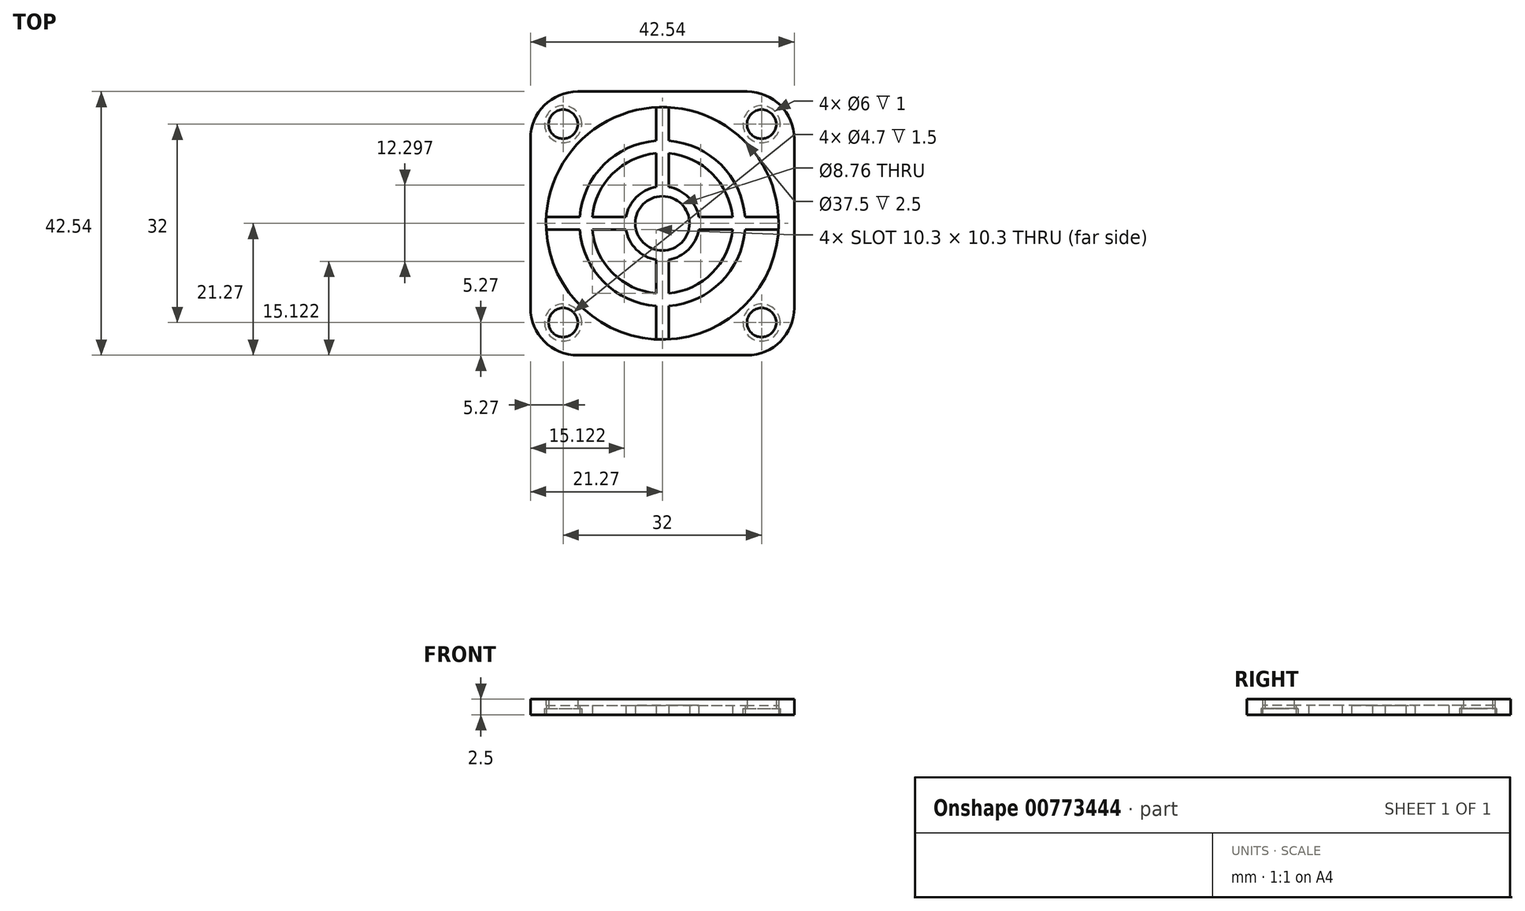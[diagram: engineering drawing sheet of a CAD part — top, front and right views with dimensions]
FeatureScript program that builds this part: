
annotation { "Feature Type Name" : "Feature", "Feature Type Description" : "" }
export const myFeature = defineFeature(function(context is Context, id is Id, definition is map)
    precondition{}
    {
        {
            var Q0;
            Q0=qCreatedBy(makeId("Top.planeOp"),FACE);
            var sketch = newSketch(context, id + "F0", { "sketchPlane" : qUnion([Q0])});
            skCircle(sketch, "E0", {"center": v(-16, 16) * mm, "radius": 1.6 * mm});
            skCircle(sketch, "E1", {"center": v(16, 16) * mm, "radius": 1.6 * mm});
            skCircle(sketch, "E2", {"center": v(16, -16) * mm, "radius": 1.6 * mm});
            skCircle(sketch, "E3", {"center": v(-16, -16) * mm, "radius": 1.6 * mm});
            skLineSegment(sketch, "E4.bottom", {"start": v(-13.65, 20) * mm, "end": v(13.65, 20) * mm});
            skLineSegment(sketch, "E4.top", {"start": v(-13.65, -20) * mm, "end": v(13.65, -20) * mm});
            skLineSegment(sketch, "E4.left", {"start": v(-20, 13.65) * mm, "end": v(-20, -13.65) * mm});
            skLineSegment(sketch, "E4.right", {"start": v(20, 13.65) * mm, "end": v(20, -13.65) * mm});
            skArc(sketch, "E5", {"start": v(-1, 18.72) * mm, "mid": v(-13.26, 13.26) * mm, "end": v(-18.72, 1) * mm});
            skLineSegment(sketch, "E6", {"start": v(-1, 18.72) * mm, "end": v(-1, 13.33) * mm});
            skLineSegment(sketch, "E7", {"start": v(1, 18.72) * mm, "end": v(1, 13.33) * mm});
            skLineSegment(sketch, "E8", {"start": v(-18.72, 1) * mm, "end": v(-13.33, 1) * mm});
            skLineSegment(sketch, "E9", {"start": v(-18.72, -1) * mm, "end": v(-13.33, -1) * mm});
            skArc(sketch, "E10.trimOffspring", {"start": v(18.72, 1) * mm, "mid": v(13.26, 13.26) * mm, "end": v(1, 18.72) * mm});
            skArc(sketch, "E11.trimOffspring", {"start": v(-18.72, -1) * mm, "mid": v(-13.26, -13.26) * mm, "end": v(-1, -18.72) * mm});
            skArc(sketch, "E12.trimOffspring", {"start": v(1, -18.72) * mm, "mid": v(13.26, -13.26) * mm, "end": v(18.72, -1) * mm});
            skArc(sketch, "E13", {"start": v(5.87, 1) * mm, "mid": v(4.21, 4.21) * mm, "end": v(1, 5.87) * mm});
            skArc(sketch, "E14", {"start": v(-1, 11.3) * mm, "mid": v(-8.02, 8.02) * mm, "end": v(-11.3, 1) * mm});
            skArc(sketch, "E15", {"start": v(-1, 13.33) * mm, "mid": v(-9.45, 9.45) * mm, "end": v(-13.33, 1) * mm});
            skLineSegment(sketch, "E16.trimOffspring", {"start": v(-1, 11.3) * mm, "end": v(-1, 5.87) * mm});
            skLineSegment(sketch, "E17.trimOffspring", {"start": v(1, 11.3) * mm, "end": v(1, 5.87) * mm});
            skLineSegment(sketch, "E18.trimOffspring", {"start": v(13.33, 1) * mm, "end": v(18.72, 1) * mm});
            skLineSegment(sketch, "E19.trimOffspring", {"start": v(13.33, -1) * mm, "end": v(18.72, -1) * mm});
            skArc(sketch, "E20.trimOffspring", {"start": v(11.3, 1) * mm, "mid": v(8.02, 8.02) * mm, "end": v(1, 11.3) * mm});
            skArc(sketch, "E21.trimOffspring", {"start": v(13.33, 1) * mm, "mid": v(9.45, 9.45) * mm, "end": v(1, 13.33) * mm});
            skLineSegment(sketch, "E22.trimOffspring", {"start": v(5.87, 1) * mm, "end": v(11.3, 1) * mm});
            skLineSegment(sketch, "E23.trimOffspring", {"start": v(5.87, -1) * mm, "end": v(11.3, -1) * mm});
            skArc(sketch, "E24.trimOffspring", {"start": v(1, -5.87) * mm, "mid": v(4.21, -4.21) * mm, "end": v(5.87, -1) * mm});
            skLineSegment(sketch, "E25.trimOffspring", {"start": v(1, -5.87) * mm, "end": v(1, -11.3) * mm});
            skLineSegment(sketch, "E26.trimOffspring", {"start": v(-1, -5.87) * mm, "end": v(-1, -11.3) * mm});
            skArc(sketch, "E27.trimOffspring", {"start": v(-5.87, -1) * mm, "mid": v(-4.21, -4.21) * mm, "end": v(-1, -5.87) * mm});
            skLineSegment(sketch, "E28.trimOffspring", {"start": v(-11.3, 1) * mm, "end": v(-5.87, 1) * mm});
            skArc(sketch, "E29.trimOffspring", {"start": v(-11.3, -1) * mm, "mid": v(-8.02, -8.02) * mm, "end": v(-1, -11.3) * mm});
            skArc(sketch, "E30.trimOffspring", {"start": v(-13.33, -1) * mm, "mid": v(-9.45, -9.45) * mm, "end": v(-1, -13.33) * mm});
            skLineSegment(sketch, "E31.trimOffspring", {"start": v(-11.3, -1) * mm, "end": v(-5.87, -1) * mm});
            skArc(sketch, "E32.trimOffspring", {"start": v(1, -11.3) * mm, "mid": v(8.02, -8.02) * mm, "end": v(11.3, -1) * mm});
            skArc(sketch, "E33.trimOffspring", {"start": v(1, -13.33) * mm, "mid": v(9.45, -9.45) * mm, "end": v(13.33, -1) * mm});
            skLineSegment(sketch, "E34.trimOffspring", {"start": v(1, -13.33) * mm, "end": v(1, -18.72) * mm});
            skLineSegment(sketch, "E35.trimOffspring", {"start": v(-1, -13.33) * mm, "end": v(-1, -18.72) * mm});
            skArc(sketch, "E36.trimOffspring", {"start": v(-1, 5.87) * mm, "mid": v(-4.21, 4.21) * mm, "end": v(-5.87, 1) * mm});
            skCircle(sketch, "E37", {"center": v(0, 0) * mm, "radius": 4.38 * mm});
            skPoint(sketch, "E38.visualSharp", {"position": v(-20, 20) * mm});
            skArc(sketch, "E38.filletArc", {"start": v(-13.65, 20) * mm, "mid": v(-18.14, 18.14) * mm, "end": v(-20, 13.65) * mm});
            skPoint(sketch, "E39.visualSharp", {"position": v(-20, -20) * mm});
            skArc(sketch, "E39.filletArc", {"start": v(-20, -13.65) * mm, "mid": v(-18.14, -18.14) * mm, "end": v(-13.65, -20) * mm});
            skPoint(sketch, "E40.visualSharp", {"position": v(20, -20) * mm});
            skArc(sketch, "E40.filletArc", {"start": v(13.65, -20) * mm, "mid": v(18.14, -18.14) * mm, "end": v(20, -13.65) * mm});
            skPoint(sketch, "E41.visualSharp", {"position": v(20, 20) * mm});
            skArc(sketch, "E41.filletArc", {"start": v(20, 13.65) * mm, "mid": v(18.14, 18.14) * mm, "end": v(13.65, 20) * mm});
            skSolve(sketch);
        }
        {
            var Q0;
            Q0=qSketchRegion(id+"F0",true);
            extrude(context, id + "F1", {"entities" : qUnion([Q0]), "depth" : 2.5 * mm, "offsetDistance" : 25.4 * mm});
        }
        {
            var Q0;
            Q0=makeQuery(id+"F1.opExtrude","CAP_FACE",FACE,{"disambiguationData":[OSD([sQuery(id+"F0.wireOp",EDGE,"E0"),sQuery(id+"F0.wireOp",EDGE,"E1"),sQuery(id+"F0.wireOp",EDGE,"E2"),sQuery(id+"F0.wireOp",EDGE,"E3"),sQuery(id+"F0.wireOp",EDGE,"E4.bottom"),sQuery(id+"F0.wireOp",EDGE,"E4.top"),sQuery(id+"F0.wireOp",EDGE,"E4.left"),sQuery(id+"F0.wireOp",EDGE,"E4.right"),sQuery(id+"F0.wireOp",EDGE,"E5"),sQuery(id+"F0.wireOp",EDGE,"E6"),sQuery(id+"F0.wireOp",EDGE,"E7"),sQuery(id+"F0.wireOp",EDGE,"E8"),sQuery(id+"F0.wireOp",EDGE,"E9"),sQuery(id+"F0.wireOp",EDGE,"3f5c4570-0d0e-4342-8f31-e9b691c76b48.trimOffspring"),sQuery(id+"F0.wireOp",EDGE,"b0981ca9-4a93-40c7-8ede-b21ccdf9ea9c.trimOffspring"),sQuery(id+"F0.wireOp",EDGE,"156f85e7-4a59-4eaa-8c94-7897f76e2177.trimOffspring"),sQuery(id+"F0.wireOp",EDGE,"7a4ee4ac-a209-40c9-a21d-254fe2efd8aa.trimOffspring"),sQuery(id+"F0.wireOp",EDGE,"E10.trimOffspring"),sQuery(id+"F0.wireOp",EDGE,"E11.trimOffspring"),sQuery(id+"F0.wireOp",EDGE,"E12.trimOffspring"),sQuery(id+"F0.wireOp",EDGE,"hUL42VZN-iO2z-RDmx-ddcc-wAsxaYuwDb2i"),sQuery(id+"F0.wireOp",EDGE,"E13"),sQuery(id+"F0.wireOp",EDGE,"E14"),sQuery(id+"F0.wireOp",EDGE,"E15"),sQuery(id+"F0.wireOp",EDGE,"E16.trimOffspring"),sQuery(id+"F0.wireOp",EDGE,"E17.trimOffspring"),sQuery(id+"F0.wireOp",EDGE,"E18.trimOffspring"),sQuery(id+"F0.wireOp",EDGE,"E19.trimOffspring"),sQuery(id+"F0.wireOp",EDGE,"E20.trimOffspring"),sQuery(id+"F0.wireOp",EDGE,"E21.trimOffspring"),sQuery(id+"F0.wireOp",EDGE,"E22.trimOffspring"),sQuery(id+"F0.wireOp",EDGE,"E23.trimOffspring"),sQuery(id+"F0.wireOp",EDGE,"E24.trimOffspring"),sQuery(id+"F0.wireOp",EDGE,"5baa72d9-31dc-45eb-b5c1-436ed97127be.trimOffspring"),sQuery(id+"F0.wireOp",EDGE,"E25.trimOffspring"),sQuery(id+"F0.wireOp",EDGE,"E26.trimOffspring"),sQuery(id+"F0.wireOp",EDGE,"923efe1c-8501-4d4e-8851-86086e94e9f1.trimOffspring"),sQuery(id+"F0.wireOp",EDGE,"3f79d5fb-0a8b-4b1f-bc07-6d58af1cd0cc.trimOffspring"),sQuery(id+"F0.wireOp",EDGE,"E27.trimOffspring"),sQuery(id+"F0.wireOp",EDGE,"26bf0d5e-ea2e-47a8-97aa-4e4c95460ec9.trimOffspring"),sQuery(id+"F0.wireOp",EDGE,"E28.trimOffspring"),sQuery(id+"F0.wireOp",EDGE,"E29.trimOffspring"),sQuery(id+"F0.wireOp",EDGE,"E30.trimOffspring"),sQuery(id+"F0.wireOp",EDGE,"E31.trimOffspring"),sQuery(id+"F0.wireOp",EDGE,"E32.trimOffspring"),sQuery(id+"F0.wireOp",EDGE,"E33.trimOffspring"),sQuery(id+"F0.wireOp",EDGE,"E34.trimOffspring"),sQuery(id+"F0.wireOp",EDGE,"E35.trimOffspring"),sQuery(id+"F0.wireOp",EDGE,"E36.trimOffspring"),sQuery(id+"F0.wireOp",EDGE,"6d97bbf4-c9fc-463e-bf00-e0ef0d70c1c3.trimOffspring"),sQuery(id+"F0.wireOp",EDGE,"3c499df6-884c-4b4b-8284-fedb37a8e2a6.trimOffspring"),sQuery(id+"F0.wireOp",EDGE,"9bf78612-3a2b-4ab4-ae83-326c1b6aaf60.trimOffspring")])],"isStart":false});
            var sketch = newSketch(context, id + "F2", { "sketchPlane" : qUnion([Q0])});
            skArc(sketch, "E42.0", {"start": v(-1, 18.72) * mm, "mid": v(-13.26, 13.26) * mm, "end": v(-18.72, 1) * mm});
            skArc(sketch, "E43.0", {"start": v(-18.72, -1) * mm, "mid": v(-13.26, -13.26) * mm, "end": v(-1, -18.72) * mm});
            skCircle(sketch, "E44", {"center": v(0, 0) * mm, "radius": 18.75 * mm});
            skSolve(sketch);
        }
        {
            var Q0;
            Q0=qSketchRegion(id+"F2",true);
            extrude(context, id + "F3", {"entities" : qUnion([Q0]), "operationType" : NewBodyOperationType.REMOVE, "oppositeDirection" : true, "depth" : 1 * mm, "offsetDistance" : 25.4 * mm});
        }
        {
            var Q0;
            Q0=makeQuery(id+"F1.opExtrude","CAP_FACE",FACE,{"disambiguationData":[OSD([sQuery(id+"F0.wireOp",EDGE,"E0"),sQuery(id+"F0.wireOp",EDGE,"E1"),sQuery(id+"F0.wireOp",EDGE,"E2"),sQuery(id+"F0.wireOp",EDGE,"E3"),sQuery(id+"F0.wireOp",EDGE,"E4.bottom"),sQuery(id+"F0.wireOp",EDGE,"E4.top"),sQuery(id+"F0.wireOp",EDGE,"E4.left"),sQuery(id+"F0.wireOp",EDGE,"E4.right"),sQuery(id+"F0.wireOp",EDGE,"E5"),sQuery(id+"F0.wireOp",EDGE,"E6"),sQuery(id+"F0.wireOp",EDGE,"E7"),sQuery(id+"F0.wireOp",EDGE,"E8"),sQuery(id+"F0.wireOp",EDGE,"E9"),sQuery(id+"F0.wireOp",EDGE,"3f5c4570-0d0e-4342-8f31-e9b691c76b48.trimOffspring"),sQuery(id+"F0.wireOp",EDGE,"b0981ca9-4a93-40c7-8ede-b21ccdf9ea9c.trimOffspring"),sQuery(id+"F0.wireOp",EDGE,"156f85e7-4a59-4eaa-8c94-7897f76e2177.trimOffspring"),sQuery(id+"F0.wireOp",EDGE,"7a4ee4ac-a209-40c9-a21d-254fe2efd8aa.trimOffspring"),sQuery(id+"F0.wireOp",EDGE,"E10.trimOffspring"),sQuery(id+"F0.wireOp",EDGE,"E11.trimOffspring"),sQuery(id+"F0.wireOp",EDGE,"E12.trimOffspring"),sQuery(id+"F0.wireOp",EDGE,"hUL42VZN-iO2z-RDmx-ddcc-wAsxaYuwDb2i"),sQuery(id+"F0.wireOp",EDGE,"E13"),sQuery(id+"F0.wireOp",EDGE,"E14"),sQuery(id+"F0.wireOp",EDGE,"E15"),sQuery(id+"F0.wireOp",EDGE,"E16.trimOffspring"),sQuery(id+"F0.wireOp",EDGE,"E17.trimOffspring"),sQuery(id+"F0.wireOp",EDGE,"E18.trimOffspring"),sQuery(id+"F0.wireOp",EDGE,"E19.trimOffspring"),sQuery(id+"F0.wireOp",EDGE,"E20.trimOffspring"),sQuery(id+"F0.wireOp",EDGE,"E21.trimOffspring"),sQuery(id+"F0.wireOp",EDGE,"E22.trimOffspring"),sQuery(id+"F0.wireOp",EDGE,"E23.trimOffspring"),sQuery(id+"F0.wireOp",EDGE,"E24.trimOffspring"),sQuery(id+"F0.wireOp",EDGE,"5baa72d9-31dc-45eb-b5c1-436ed97127be.trimOffspring"),sQuery(id+"F0.wireOp",EDGE,"E25.trimOffspring"),sQuery(id+"F0.wireOp",EDGE,"E26.trimOffspring"),sQuery(id+"F0.wireOp",EDGE,"923efe1c-8501-4d4e-8851-86086e94e9f1.trimOffspring"),sQuery(id+"F0.wireOp",EDGE,"3f79d5fb-0a8b-4b1f-bc07-6d58af1cd0cc.trimOffspring"),sQuery(id+"F0.wireOp",EDGE,"E27.trimOffspring"),sQuery(id+"F0.wireOp",EDGE,"26bf0d5e-ea2e-47a8-97aa-4e4c95460ec9.trimOffspring"),sQuery(id+"F0.wireOp",EDGE,"E28.trimOffspring"),sQuery(id+"F0.wireOp",EDGE,"E29.trimOffspring"),sQuery(id+"F0.wireOp",EDGE,"E30.trimOffspring"),sQuery(id+"F0.wireOp",EDGE,"E31.trimOffspring"),sQuery(id+"F0.wireOp",EDGE,"E32.trimOffspring"),sQuery(id+"F0.wireOp",EDGE,"E33.trimOffspring"),sQuery(id+"F0.wireOp",EDGE,"E34.trimOffspring"),sQuery(id+"F0.wireOp",EDGE,"E35.trimOffspring"),sQuery(id+"F0.wireOp",EDGE,"E36.trimOffspring"),sQuery(id+"F0.wireOp",EDGE,"6d97bbf4-c9fc-463e-bf00-e0ef0d70c1c3.trimOffspring"),sQuery(id+"F0.wireOp",EDGE,"3c499df6-884c-4b4b-8284-fedb37a8e2a6.trimOffspring"),sQuery(id+"F0.wireOp",EDGE,"9bf78612-3a2b-4ab4-ae83-326c1b6aaf60.trimOffspring")])],"isStart":true});
            var sketch = newSketch(context, id + "F4", { "sketchPlane" : qUnion([Q0])});
            skCircle(sketch, "E45.0", {"center": v(-16, -16) * mm, "radius": 1.6 * mm});
            skCircle(sketch, "E46.0", {"center": v(16, -16) * mm, "radius": 1.6 * mm});
            skCircle(sketch, "E47.0", {"center": v(16, 16) * mm, "radius": 1.6 * mm});
            skCircle(sketch, "E48.0", {"center": v(-16, 16) * mm, "radius": 1.6 * mm});
            skCircle(sketch, "E49", {"center": v(-16, 16) * mm, "radius": 3 * mm});
            skCircle(sketch, "E50", {"center": v(16, 16) * mm, "radius": 3 * mm});
            skCircle(sketch, "E51", {"center": v(16, -16) * mm, "radius": 3 * mm});
            skCircle(sketch, "E52", {"center": v(-16, -16) * mm, "radius": 3 * mm});
            skSolve(sketch);
        }
        {
            var Q0;
            Q0=qSketchRegion(id+"F4",true);
            extrude(context, id + "F5", {"entities" : qUnion([Q0]), "operationType" : NewBodyOperationType.REMOVE, "oppositeDirection" : true, "depth" : 1 * mm, "offsetDistance" : 25.4 * mm});
        }
        {
            var Q0;
            Q0=makeQuery(id+"F1.opExtrude","CAP_FACE",FACE,{"disambiguationData":[OSD([sQuery(id+"F0.wireOp",EDGE,"E0"),sQuery(id+"F0.wireOp",EDGE,"E1"),sQuery(id+"F0.wireOp",EDGE,"E2"),sQuery(id+"F0.wireOp",EDGE,"E3"),sQuery(id+"F0.wireOp",EDGE,"E4.bottom"),sQuery(id+"F0.wireOp",EDGE,"E4.top"),sQuery(id+"F0.wireOp",EDGE,"E4.left"),sQuery(id+"F0.wireOp",EDGE,"E4.right"),sQuery(id+"F0.wireOp",EDGE,"E5"),sQuery(id+"F0.wireOp",EDGE,"E6"),sQuery(id+"F0.wireOp",EDGE,"E7"),sQuery(id+"F0.wireOp",EDGE,"E8"),sQuery(id+"F0.wireOp",EDGE,"E9"),sQuery(id+"F0.wireOp",EDGE,"E10.trimOffspring"),sQuery(id+"F0.wireOp",EDGE,"E11.trimOffspring"),sQuery(id+"F0.wireOp",EDGE,"E12.trimOffspring"),sQuery(id+"F0.wireOp",EDGE,"E13"),sQuery(id+"F0.wireOp",EDGE,"E14"),sQuery(id+"F0.wireOp",EDGE,"E15"),sQuery(id+"F0.wireOp",EDGE,"E16.trimOffspring"),sQuery(id+"F0.wireOp",EDGE,"E17.trimOffspring"),sQuery(id+"F0.wireOp",EDGE,"E18.trimOffspring"),sQuery(id+"F0.wireOp",EDGE,"E19.trimOffspring"),sQuery(id+"F0.wireOp",EDGE,"E20.trimOffspring"),sQuery(id+"F0.wireOp",EDGE,"E21.trimOffspring"),sQuery(id+"F0.wireOp",EDGE,"E22.trimOffspring"),sQuery(id+"F0.wireOp",EDGE,"E23.trimOffspring"),sQuery(id+"F0.wireOp",EDGE,"E24.trimOffspring"),sQuery(id+"F0.wireOp",EDGE,"E25.trimOffspring"),sQuery(id+"F0.wireOp",EDGE,"E26.trimOffspring"),sQuery(id+"F0.wireOp",EDGE,"E27.trimOffspring"),sQuery(id+"F0.wireOp",EDGE,"E28.trimOffspring"),sQuery(id+"F0.wireOp",EDGE,"E29.trimOffspring"),sQuery(id+"F0.wireOp",EDGE,"E30.trimOffspring"),sQuery(id+"F0.wireOp",EDGE,"E31.trimOffspring"),sQuery(id+"F0.wireOp",EDGE,"E32.trimOffspring"),sQuery(id+"F0.wireOp",EDGE,"E33.trimOffspring"),sQuery(id+"F0.wireOp",EDGE,"E34.trimOffspring"),sQuery(id+"F0.wireOp",EDGE,"E35.trimOffspring"),sQuery(id+"F0.wireOp",EDGE,"E36.trimOffspring"),sQuery(id+"F0.wireOp",EDGE,"E37"),sQuery(id+"F0.wireOp",EDGE,"E38.filletArc"),sQuery(id+"F0.wireOp",EDGE,"E39.filletArc"),sQuery(id+"F0.wireOp",EDGE,"E40.filletArc"),sQuery(id+"F0.wireOp",EDGE,"E41.filletArc")])],"isStart":true});
            var sketch = newSketch(context, id + "F6", { "sketchPlane" : qUnion([Q0])});
            skLineSegment(sketch, "E53.0", {"start": v(-13.65, 20) * mm, "end": v(13.65, 20) * mm});
            skArc(sketch, "E54.0", {"start": v(-20, 13.65) * mm, "mid": v(-18.14, 18.14) * mm, "end": v(-13.65, 20) * mm});
            skLineSegment(sketch, "E55.0", {"start": v(-20, -13.65) * mm, "end": v(-20, 13.65) * mm});
            skArc(sketch, "E56.0", {"start": v(-13.65, -20) * mm, "mid": v(-18.14, -18.14) * mm, "end": v(-20, -13.65) * mm});
            skLineSegment(sketch, "E57.0", {"start": v(-13.65, -20) * mm, "end": v(13.65, -20) * mm});
            skArc(sketch, "E58.0", {"start": v(20, -13.65) * mm, "mid": v(18.14, -18.14) * mm, "end": v(13.65, -20) * mm});
            skLineSegment(sketch, "E59.0", {"start": v(20, -13.65) * mm, "end": v(20, 13.65) * mm});
            skArc(sketch, "E60.0", {"start": v(13.65, 20) * mm, "mid": v(18.14, 18.14) * mm, "end": v(20, 13.65) * mm});
            skArc(sketch, "E61.0", {"start": v(-21.27, 13.65) * mm, "mid": v(-19.04, 19.04) * mm, "end": v(-13.65, 21.27) * mm});
            skLineSegment(sketch, "E61.1", {"start": v(-21.27, -13.65) * mm, "end": v(-21.27, 13.65) * mm});
            skLineSegment(sketch, "E61.2", {"start": v(-13.65, 21.27) * mm, "end": v(13.65, 21.27) * mm});
            skArc(sketch, "E61.3", {"start": v(-13.65, -21.27) * mm, "mid": v(-19.04, -19.04) * mm, "end": v(-21.27, -13.65) * mm});
            skArc(sketch, "E61.4", {"start": v(13.65, 21.27) * mm, "mid": v(19.04, 19.04) * mm, "end": v(21.27, 13.65) * mm});
            skLineSegment(sketch, "E61.5", {"start": v(21.27, -13.65) * mm, "end": v(21.27, 13.65) * mm});
            skArc(sketch, "E61.6", {"start": v(21.27, -13.65) * mm, "mid": v(19.04, -19.04) * mm, "end": v(13.65, -21.27) * mm});
            skLineSegment(sketch, "E61.7", {"start": v(-13.65, -21.27) * mm, "end": v(13.65, -21.27) * mm});
            skSolve(sketch);
        }
        {
            var Q0;
            Q0=qSketchRegion(id+"F6",true);
            var Q1;
            Q1=makeQuery(id+"F1.opExtrude","CAP_FACE",FACE,{"disambiguationData":[OSD([sQuery(id+"F0.wireOp",EDGE,"E0"),sQuery(id+"F0.wireOp",EDGE,"E1"),sQuery(id+"F0.wireOp",EDGE,"E2"),sQuery(id+"F0.wireOp",EDGE,"E3"),sQuery(id+"F0.wireOp",EDGE,"E4.bottom"),sQuery(id+"F0.wireOp",EDGE,"E4.top"),sQuery(id+"F0.wireOp",EDGE,"E4.left"),sQuery(id+"F0.wireOp",EDGE,"E4.right"),sQuery(id+"F0.wireOp",EDGE,"E5"),sQuery(id+"F0.wireOp",EDGE,"E6"),sQuery(id+"F0.wireOp",EDGE,"E7"),sQuery(id+"F0.wireOp",EDGE,"E8"),sQuery(id+"F0.wireOp",EDGE,"E9"),sQuery(id+"F0.wireOp",EDGE,"E10.trimOffspring"),sQuery(id+"F0.wireOp",EDGE,"E11.trimOffspring"),sQuery(id+"F0.wireOp",EDGE,"E12.trimOffspring"),sQuery(id+"F0.wireOp",EDGE,"E13"),sQuery(id+"F0.wireOp",EDGE,"E14"),sQuery(id+"F0.wireOp",EDGE,"E15"),sQuery(id+"F0.wireOp",EDGE,"E16.trimOffspring"),sQuery(id+"F0.wireOp",EDGE,"E17.trimOffspring"),sQuery(id+"F0.wireOp",EDGE,"E18.trimOffspring"),sQuery(id+"F0.wireOp",EDGE,"E19.trimOffspring"),sQuery(id+"F0.wireOp",EDGE,"E20.trimOffspring"),sQuery(id+"F0.wireOp",EDGE,"E21.trimOffspring"),sQuery(id+"F0.wireOp",EDGE,"E22.trimOffspring"),sQuery(id+"F0.wireOp",EDGE,"E23.trimOffspring"),sQuery(id+"F0.wireOp",EDGE,"E24.trimOffspring"),sQuery(id+"F0.wireOp",EDGE,"E25.trimOffspring"),sQuery(id+"F0.wireOp",EDGE,"E26.trimOffspring"),sQuery(id+"F0.wireOp",EDGE,"E27.trimOffspring"),sQuery(id+"F0.wireOp",EDGE,"E28.trimOffspring"),sQuery(id+"F0.wireOp",EDGE,"E29.trimOffspring"),sQuery(id+"F0.wireOp",EDGE,"E30.trimOffspring"),sQuery(id+"F0.wireOp",EDGE,"E31.trimOffspring"),sQuery(id+"F0.wireOp",EDGE,"E32.trimOffspring"),sQuery(id+"F0.wireOp",EDGE,"E33.trimOffspring"),sQuery(id+"F0.wireOp",EDGE,"E34.trimOffspring"),sQuery(id+"F0.wireOp",EDGE,"E35.trimOffspring"),sQuery(id+"F0.wireOp",EDGE,"E36.trimOffspring"),sQuery(id+"F0.wireOp",EDGE,"E37"),sQuery(id+"F0.wireOp",EDGE,"E38.filletArc"),sQuery(id+"F0.wireOp",EDGE,"E39.filletArc"),sQuery(id+"F0.wireOp",EDGE,"E40.filletArc"),sQuery(id+"F0.wireOp",EDGE,"E41.filletArc")])],"isStart":false});
            extrude(context, id + "F7", {"entities" : qUnion([Q0]), "operationType" : NewBodyOperationType.ADD, "endBound" : BoundingType.UP_TO_SURFACE, "oppositeDirection" : true, "depth" : 25.4 * mm, "endBoundEntityFace" : qUnion([Q1]), "offsetDistance" : 25.4 * mm});
        }
        {
            var Q0;
            Q0=makeQuery(id+"F7.boolean.opBoolean","MERGE",FACE,{"derivedFrom":[makeQuery(id+"F1.opExtrude","CAP_FACE",FACE,{"disambiguationData":[OSD([sQuery(id+"F0.wireOp",EDGE,"E0"),sQuery(id+"F0.wireOp",EDGE,"E1"),sQuery(id+"F0.wireOp",EDGE,"E2"),sQuery(id+"F0.wireOp",EDGE,"E3"),sQuery(id+"F0.wireOp",EDGE,"E4.bottom"),sQuery(id+"F0.wireOp",EDGE,"E4.top"),sQuery(id+"F0.wireOp",EDGE,"E4.left"),sQuery(id+"F0.wireOp",EDGE,"E4.right"),sQuery(id+"F0.wireOp",EDGE,"E5"),sQuery(id+"F0.wireOp",EDGE,"E6"),sQuery(id+"F0.wireOp",EDGE,"E7"),sQuery(id+"F0.wireOp",EDGE,"E8"),sQuery(id+"F0.wireOp",EDGE,"E9"),sQuery(id+"F0.wireOp",EDGE,"E10.trimOffspring"),sQuery(id+"F0.wireOp",EDGE,"E11.trimOffspring"),sQuery(id+"F0.wireOp",EDGE,"E12.trimOffspring"),sQuery(id+"F0.wireOp",EDGE,"E13"),sQuery(id+"F0.wireOp",EDGE,"E14"),sQuery(id+"F0.wireOp",EDGE,"E15"),sQuery(id+"F0.wireOp",EDGE,"E16.trimOffspring"),sQuery(id+"F0.wireOp",EDGE,"E17.trimOffspring"),sQuery(id+"F0.wireOp",EDGE,"E18.trimOffspring"),sQuery(id+"F0.wireOp",EDGE,"E19.trimOffspring"),sQuery(id+"F0.wireOp",EDGE,"E20.trimOffspring"),sQuery(id+"F0.wireOp",EDGE,"E21.trimOffspring"),sQuery(id+"F0.wireOp",EDGE,"E22.trimOffspring"),sQuery(id+"F0.wireOp",EDGE,"E23.trimOffspring"),sQuery(id+"F0.wireOp",EDGE,"E24.trimOffspring"),sQuery(id+"F0.wireOp",EDGE,"E25.trimOffspring"),sQuery(id+"F0.wireOp",EDGE,"E26.trimOffspring"),sQuery(id+"F0.wireOp",EDGE,"E27.trimOffspring"),sQuery(id+"F0.wireOp",EDGE,"E28.trimOffspring"),sQuery(id+"F0.wireOp",EDGE,"E29.trimOffspring"),sQuery(id+"F0.wireOp",EDGE,"E30.trimOffspring"),sQuery(id+"F0.wireOp",EDGE,"E31.trimOffspring"),sQuery(id+"F0.wireOp",EDGE,"E32.trimOffspring"),sQuery(id+"F0.wireOp",EDGE,"E33.trimOffspring"),sQuery(id+"F0.wireOp",EDGE,"E34.trimOffspring"),sQuery(id+"F0.wireOp",EDGE,"E35.trimOffspring"),sQuery(id+"F0.wireOp",EDGE,"E36.trimOffspring"),sQuery(id+"F0.wireOp",EDGE,"E37"),sQuery(id+"F0.wireOp",EDGE,"E38.filletArc"),sQuery(id+"F0.wireOp",EDGE,"E39.filletArc"),sQuery(id+"F0.wireOp",EDGE,"E40.filletArc"),sQuery(id+"F0.wireOp",EDGE,"E41.filletArc")])],"isStart":false}),makeQuery(id+"F7.opExtrude","CAP_FACE",FACE,{"disambiguationData":[OSD([sQuery(id+"F6.wireOp",EDGE,"E53.0"),sQuery(id+"F6.wireOp",EDGE,"E54.0"),sQuery(id+"F6.wireOp",EDGE,"E55.0"),sQuery(id+"F6.wireOp",EDGE,"E56.0"),sQuery(id+"F6.wireOp",EDGE,"E57.0"),sQuery(id+"F6.wireOp",EDGE,"E58.0"),sQuery(id+"F6.wireOp",EDGE,"E59.0"),sQuery(id+"F6.wireOp",EDGE,"E60.0"),sQuery(id+"F6.wireOp",EDGE,"E61.0"),sQuery(id+"F6.wireOp",EDGE,"E61.1"),sQuery(id+"F6.wireOp",EDGE,"E61.2"),sQuery(id+"F6.wireOp",EDGE,"E61.3"),sQuery(id+"F6.wireOp",EDGE,"E61.4"),sQuery(id+"F6.wireOp",EDGE,"E61.5"),sQuery(id+"F6.wireOp",EDGE,"E61.6"),sQuery(id+"F6.wireOp",EDGE,"E61.7")])],"isStart":false})]});
            var sketch = newSketch(context, id + "F8", { "sketchPlane" : qUnion([Q0])});
            skCircle(sketch, "E62.0", {"center": v(16, -16) * mm, "radius": 1.6 * mm, "construction": true});
            skCircle(sketch, "E63.0", {"center": v(-16, -16) * mm, "radius": 1.6 * mm, "construction": true});
            skCircle(sketch, "E64.0", {"center": v(16, 16) * mm, "radius": 1.6 * mm, "construction": true});
            skCircle(sketch, "E65.0", {"center": v(-16, 16) * mm, "radius": 1.6 * mm, "construction": true});
            skCircle(sketch, "E66", {"center": v(16, 16) * mm, "radius": 1.7 * mm});
            skCircle(sketch, "E67", {"center": v(16, -16) * mm, "radius": 1.7 * mm});
            skCircle(sketch, "E68", {"center": v(-16, -16) * mm, "radius": 1.7 * mm});
            skCircle(sketch, "E69", {"center": v(-16, 16) * mm, "radius": 1.7 * mm});
            skSolve(sketch);
        }
        {
            var Q0;
            Q0=qSketchRegion(id+"F8",true);
            extrude(context, id + "F9", {"entities" : qUnion([Q0]), "operationType" : NewBodyOperationType.REMOVE, "endBound" : BoundingType.THROUGH_ALL, "oppositeDirection" : true, "depth" : 25 * mm, "offsetDistance" : 25 * mm});
        }
        {
            var Q0;
            Q0=sQuery(id+"F4.wireOp",VERTEX,"E45.0.center");
            var Q1;
            Q1=sQuery(id+"F4.wireOp",VERTEX,"E46.0.center");
            var Q2;
            Q2=sQuery(id+"F4.wireOp",VERTEX,"E47.0.center");
            var Q3;
            Q3=sQuery(id+"F4.wireOp",VERTEX,"E48.0.center");
            var Q4;
            Q4=makeQuery(id+"F1.opExtrude","SWEPT_BODY",BODY,{"disambiguationData":[OSD([sQuery(id+"F0.wireOp",EDGE,"E0"),sQuery(id+"F0.wireOp",EDGE,"E1"),sQuery(id+"F0.wireOp",EDGE,"E2"),sQuery(id+"F0.wireOp",EDGE,"E3"),sQuery(id+"F0.wireOp",EDGE,"E4.bottom"),sQuery(id+"F0.wireOp",EDGE,"E4.top"),sQuery(id+"F0.wireOp",EDGE,"E4.left"),sQuery(id+"F0.wireOp",EDGE,"E4.right"),sQuery(id+"F0.wireOp",EDGE,"E5"),sQuery(id+"F0.wireOp",EDGE,"E6"),sQuery(id+"F0.wireOp",EDGE,"E7"),sQuery(id+"F0.wireOp",EDGE,"E8"),sQuery(id+"F0.wireOp",EDGE,"E9"),sQuery(id+"F0.wireOp",EDGE,"E10.trimOffspring"),sQuery(id+"F0.wireOp",EDGE,"E11.trimOffspring"),sQuery(id+"F0.wireOp",EDGE,"E12.trimOffspring"),sQuery(id+"F0.wireOp",EDGE,"E13"),sQuery(id+"F0.wireOp",EDGE,"E14"),sQuery(id+"F0.wireOp",EDGE,"E15"),sQuery(id+"F0.wireOp",EDGE,"E16.trimOffspring"),sQuery(id+"F0.wireOp",EDGE,"E17.trimOffspring"),sQuery(id+"F0.wireOp",EDGE,"E18.trimOffspring"),sQuery(id+"F0.wireOp",EDGE,"E19.trimOffspring"),sQuery(id+"F0.wireOp",EDGE,"E20.trimOffspring"),sQuery(id+"F0.wireOp",EDGE,"E21.trimOffspring"),sQuery(id+"F0.wireOp",EDGE,"E22.trimOffspring"),sQuery(id+"F0.wireOp",EDGE,"E23.trimOffspring"),sQuery(id+"F0.wireOp",EDGE,"E24.trimOffspring"),sQuery(id+"F0.wireOp",EDGE,"E25.trimOffspring"),sQuery(id+"F0.wireOp",EDGE,"E26.trimOffspring"),sQuery(id+"F0.wireOp",EDGE,"E27.trimOffspring"),sQuery(id+"F0.wireOp",EDGE,"E28.trimOffspring"),sQuery(id+"F0.wireOp",EDGE,"E29.trimOffspring"),sQuery(id+"F0.wireOp",EDGE,"E30.trimOffspring"),sQuery(id+"F0.wireOp",EDGE,"E31.trimOffspring"),sQuery(id+"F0.wireOp",EDGE,"E32.trimOffspring"),sQuery(id+"F0.wireOp",EDGE,"E33.trimOffspring"),sQuery(id+"F0.wireOp",EDGE,"E34.trimOffspring"),sQuery(id+"F0.wireOp",EDGE,"E35.trimOffspring"),sQuery(id+"F0.wireOp",EDGE,"E36.trimOffspring"),sQuery(id+"F0.wireOp",EDGE,"E37"),sQuery(id+"F0.wireOp",EDGE,"E38.filletArc"),sQuery(id+"F0.wireOp",EDGE,"E39.filletArc"),sQuery(id+"F0.wireOp",EDGE,"E40.filletArc"),sQuery(id+"F0.wireOp",EDGE,"E41.filletArc")])]});
            hole(context, id + "F10", {"style" : HoleStyle.SIMPLE, "endStyle" : HoleEndStyle.THROUGH, "holeDiameter" : 4.7 * mm, "majorDiameter" : 5 * mm, "tappedDepth" : 12 * mm, "tapClearance" : 3, "startFromSketch" : true, "locations" : qUnion([Q0, Q1, Q2, Q3]), "scope" : qUnion([Q4])});
        }
    });
